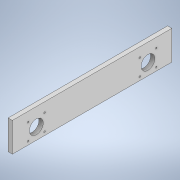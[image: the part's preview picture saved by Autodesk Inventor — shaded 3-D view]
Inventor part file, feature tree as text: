
AUTODESK INVENTOR PART (.ipt)
format: ipt  version: 2020 (Build 240168000, 168)  size: 120,320 bytes
history: native  units: mm
features: other x1, extrude x1, sketch x1
ambient origin geometry x8: Origin, YZ Plane, XZ Plane, XY Plane, X Axis, Y Axis, Z Axis, Center Point
bodies: Body1 (feature_tree)
feature tree (3):
  other  "Bryła1"
  extrude  "Wyciągnięcie proste1"  Depth=300.0mm
  sketch  "Szkic1"
